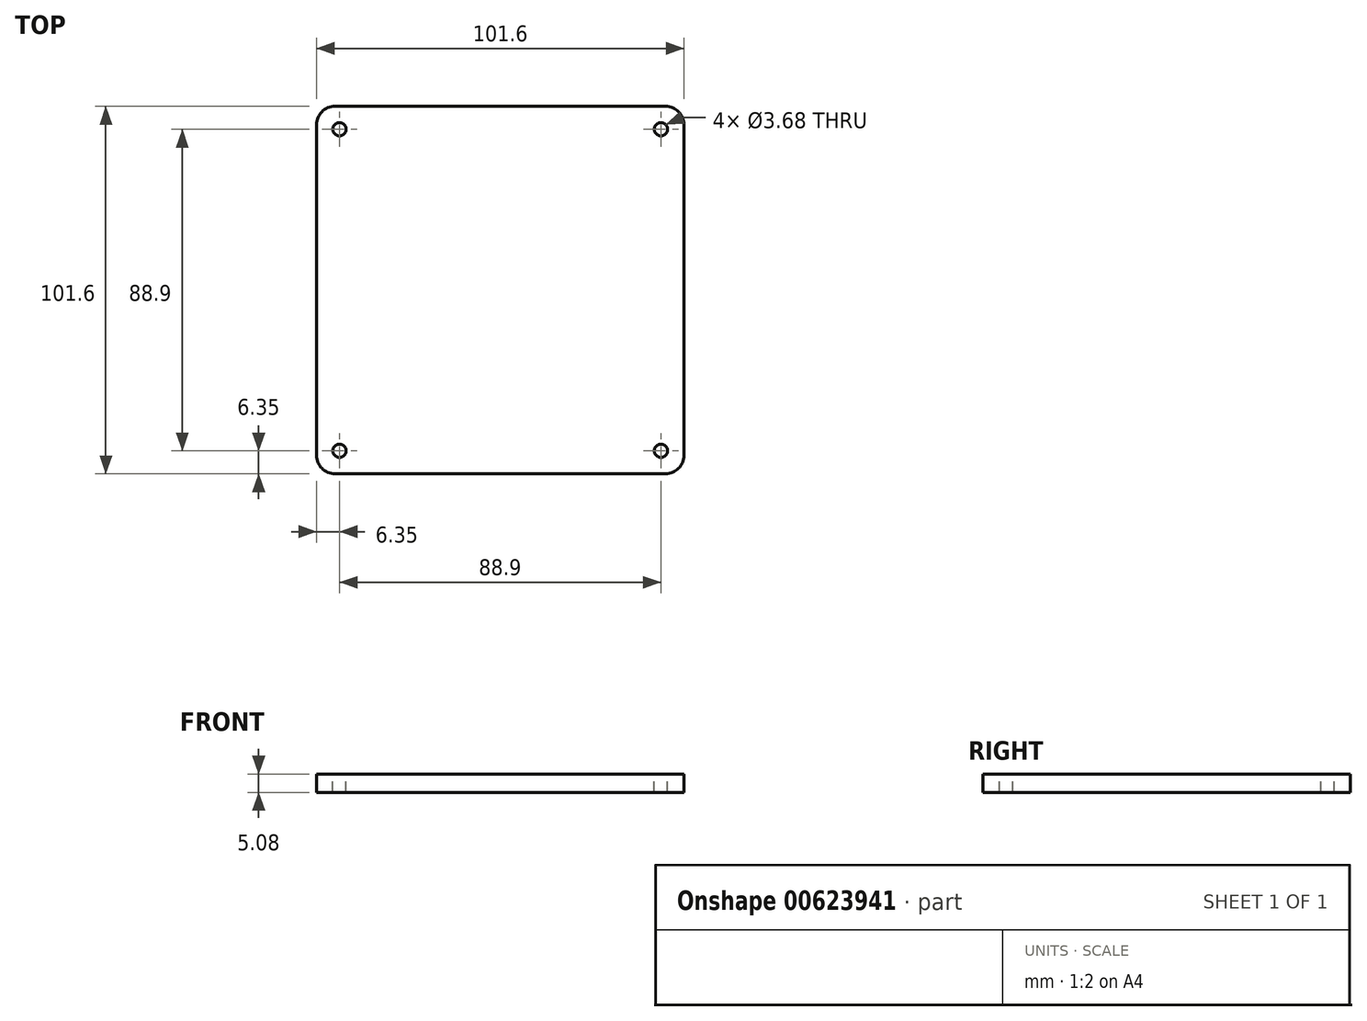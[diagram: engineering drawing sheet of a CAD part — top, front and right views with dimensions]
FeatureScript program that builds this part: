
annotation { "Feature Type Name" : "Feature", "Feature Type Description" : "" }
export const myFeature = defineFeature(function(context is Context, id is Id, definition is map)
    precondition{}
    {
        {
            var Q0;
            Q0=qCreatedBy(makeId("Top.planeOp"),FACE);
            var sketch = newSketch(context, id + "F0", { "sketchPlane" : qUnion([Q0])});
            skLineSegment(sketch, "E0.bottom", {"start": v(0, 0) * mm, "end": v(101.6, 0) * mm});
            skLineSegment(sketch, "E0.top", {"start": v(0, 101.6) * mm, "end": v(101.6, 101.6) * mm});
            skLineSegment(sketch, "E0.left", {"start": v(0, 0) * mm, "end": v(0, 101.6) * mm});
            skLineSegment(sketch, "E0.right", {"start": v(101.6, 0) * mm, "end": v(101.6, 101.6) * mm});
            skSolve(sketch);
        }
        {
            var Q0;
            Q0=qSketchRegion(id+"F0",true);
            extrude(context, id + "F1", {"entities" : qUnion([Q0]), "depth" : 5.08 * mm});
        }
        {
            var Q0;
            Q0=makeQuery(id+"F1.opExtrude","CAP_FACE",FACE,{"disambiguationData":[OSD([sQuery(id+"F0.wireOp",EDGE,"E0.bottom"),sQuery(id+"F0.wireOp",EDGE,"E0.top"),sQuery(id+"F0.wireOp",EDGE,"E0.left"),sQuery(id+"F0.wireOp",EDGE,"E0.right")])],"isStart":false});
            var sketch = newSketch(context, id + "F2", { "sketchPlane" : qUnion([Q0])});
            skLineSegment(sketch, "E1.bottom", {"start": v(6.35, 95.25) * mm, "end": v(95.25, 95.25) * mm, "construction": true});
            skLineSegment(sketch, "E1.top", {"start": v(6.35, 6.35) * mm, "end": v(95.25, 6.35) * mm, "construction": true});
            skLineSegment(sketch, "E1.left", {"start": v(6.35, 95.25) * mm, "end": v(6.35, 6.35) * mm, "construction": true});
            skLineSegment(sketch, "E1.right", {"start": v(95.25, 95.25) * mm, "end": v(95.25, 6.35) * mm, "construction": true});
            skCircle(sketch, "E2", {"center": v(6.35, 95.25) * mm, "radius": 1.84 * mm});
            skCircle(sketch, "E3", {"center": v(95.25, 95.25) * mm, "radius": 1.84 * mm});
            skCircle(sketch, "E4", {"center": v(95.25, 6.35) * mm, "radius": 1.84 * mm});
            skCircle(sketch, "E5", {"center": v(6.35, 6.35) * mm, "radius": 1.84 * mm});
            skSolve(sketch);
        }
        {
            var Q0;
            Q0=qSketchRegion(id+"F2",true);
            extrude(context, id + "F3", {"entities" : qUnion([Q0]), "operationType" : NewBodyOperationType.REMOVE, "endBound" : BoundingType.THROUGH_ALL, "oppositeDirection" : true, "depth" : 25.4 * mm});
        }
        {
            var Q0;
            Q0=makeQuery(id+"F1.opExtrude","SWEPT_EDGE",EDGE,{"disambiguationData":[OSD([sQuery(id+"F0.wireOp",EDGE,"E0.bottom"),sQuery(id+"F0.wireOp",EDGE,"E0.left")])]});
            var Q1;
            Q1=makeQuery(id+"F1.opExtrude","SWEPT_EDGE",EDGE,{"disambiguationData":[OSD([sQuery(id+"F0.wireOp",EDGE,"E0.bottom"),sQuery(id+"F0.wireOp",EDGE,"E0.right")])]});
            var Q2;
            Q2=makeQuery(id+"F1.opExtrude","SWEPT_EDGE",EDGE,{"disambiguationData":[OSD([sQuery(id+"F0.wireOp",EDGE,"E0.top"),sQuery(id+"F0.wireOp",EDGE,"E0.right")])]});
            var Q3;
            Q3=makeQuery(id+"F1.opExtrude","SWEPT_EDGE",EDGE,{"disambiguationData":[OSD([sQuery(id+"F0.wireOp",EDGE,"E0.top"),sQuery(id+"F0.wireOp",EDGE,"E0.left")])]});
            fillet(context, id + "F4", {"entities" : qUnion([Q0, Q1, Q2, Q3]), "radius" : 5.08 * mm, "tangentPropagation" : true, "allowEdgeOverflow" : false});
        }
    });
